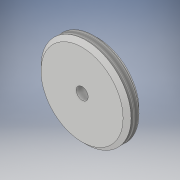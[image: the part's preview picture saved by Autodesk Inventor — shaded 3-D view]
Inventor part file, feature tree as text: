
AUTODESK INVENTOR PART (.ipt)
format: ipt  version: 2019 (Build 230136000, 136)  size: 111,104 bytes
history: native  units: mm
features: sketch x2, extrude x1, thread x1, chamfer x1, hole x1
ambient origin geometry x8: Origin, YZ Plane, XZ Plane, XY Plane, X Axis, Y Axis, Z Axis, Center Point
bodies: Solid1 (feature_tree)
feature tree (6):
  extrude  "Extrusion1"  Depth=20.0mm TaperAngle=0.0deg
  thread  "Thread1"  [1 undecoded]
  chamfer  "Chamfer1"  Distance=5.0mm Angle=45.0deg
  hole  "Hole1"  [1 undecoded]
  sketch  "Sketch1"  dims[d0=113.0mm d1=20.0mm d2=0.0mm d3=10.0mm d4=0.0mm d5=5.0mm d6=2.0mm d7=45.0deg]
  sketch  "Sketch2"  dims[d8=15.0mm d9=6.0mm d10=4.0mm d11=2.0mm d12=90.0deg d13=20.0mm d14=20.594885mm]
note: 2 required parameter values undecoded (feature->parameter linkage not recoverable at this tier; creation-order binding heuristic only, values carry confidence <= 0.55)
